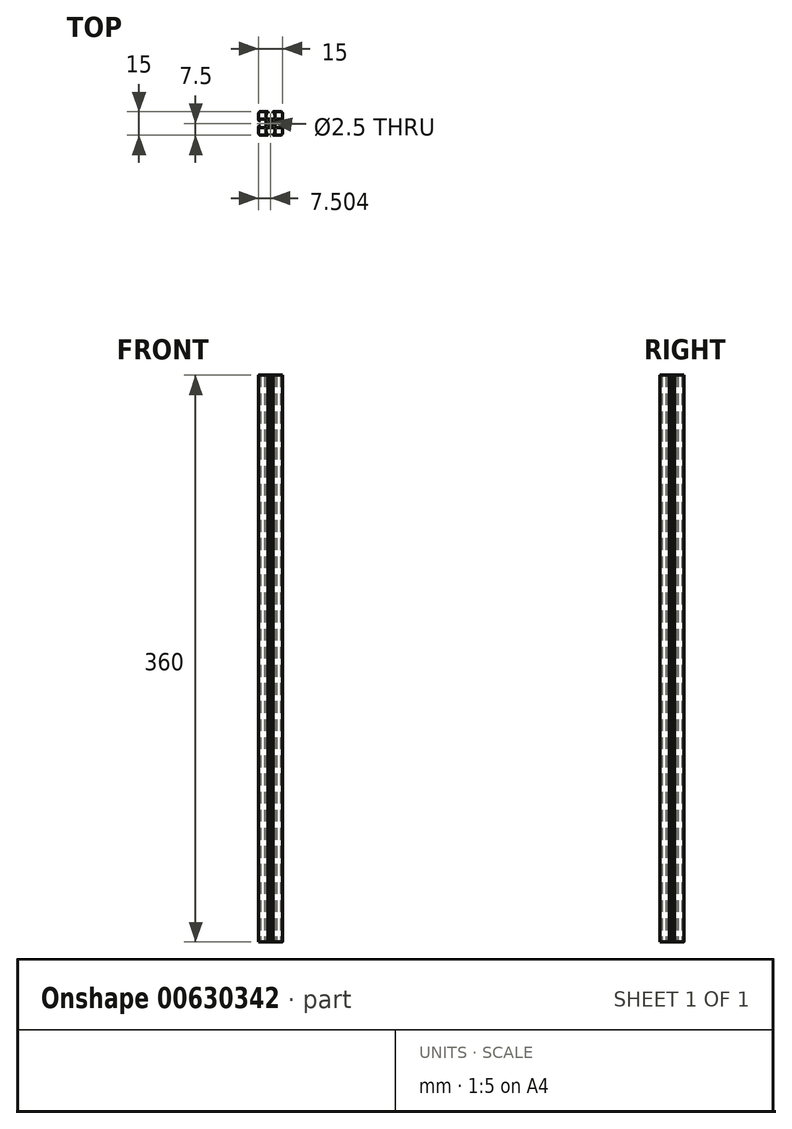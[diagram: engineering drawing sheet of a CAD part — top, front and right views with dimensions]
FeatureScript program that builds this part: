
annotation { "Feature Type Name" : "Feature", "Feature Type Description" : "" }
export const myFeature = defineFeature(function(context is Context, id is Id, definition is map)
    precondition{}
    {
        {
            var Q0;
            Q0=qCreatedBy(makeId("Top.planeOp"),FACE);
            var sketch = newSketch(context, id + "F0", { "sketchPlane" : qUnion([Q0])});
            skLineSegment(sketch, "E0", {"start": v(-5.54, -0.25) * mm, "end": v(-2.91, -0.25) * mm});
            skLineSegment(sketch, "E1", {"start": v(-4.23, -1.56) * mm, "end": v(-4.23, 1.06) * mm});
            skLineSegment(sketch, "E2", {"start": v(-11.73, 6.25) * mm, "end": v(-11.73, 1.75) * mm});
            skArc(sketch, "E3", {"start": v(-11.73, 1.75) * mm, "mid": v(-11.64, 1.54) * mm, "end": v(-11.43, 1.45) * mm});
            skLineSegment(sketch, "E4", {"start": v(-11.43, 1.45) * mm, "end": v(-10.63, 1.45) * mm});
            skLineSegment(sketch, "E5", {"start": v(-10.63, 1.45) * mm, "end": v(-10.63, 2.6) * mm});
            skLineSegment(sketch, "E6", {"start": v(-10.63, 2.6) * mm, "end": v(-8.03, 2.6) * mm});
            skLineSegment(sketch, "E7", {"start": v(-8.03, 2.6) * mm, "end": v(-7.03, 1.6) * mm});
            skLineSegment(sketch, "E8", {"start": v(-7.03, 1.6) * mm, "end": v(-7.03, 0.27) * mm});
            skLineSegment(sketch, "E9", {"start": v(-7.03, 0.27) * mm, "end": v(-6.73, -0.25) * mm});
            skLineSegment(sketch, "E10", {"start": v(-6.73, -0.25) * mm, "end": v(-7.03, -0.77) * mm});
            skLineSegment(sketch, "E11", {"start": v(-7.03, -0.77) * mm, "end": v(-7.03, -2.1) * mm});
            skLineSegment(sketch, "E12", {"start": v(-7.03, -2.1) * mm, "end": v(-8.03, -3.1) * mm});
            skLineSegment(sketch, "E13", {"start": v(-8.03, -3.1) * mm, "end": v(-10.63, -3.1) * mm});
            skLineSegment(sketch, "E14", {"start": v(-10.63, -3.1) * mm, "end": v(-10.63, -1.95) * mm});
            skLineSegment(sketch, "E15", {"start": v(-10.63, -1.95) * mm, "end": v(-11.43, -1.95) * mm});
            skArc(sketch, "E16", {"start": v(-11.43, -1.95) * mm, "mid": v(-11.64, -2.04) * mm, "end": v(-11.73, -2.25) * mm});
            skLineSegment(sketch, "E17", {"start": v(-11.73, -2.25) * mm, "end": v(-11.73, -6.75) * mm});
            skArc(sketch, "E18", {"start": v(-11.73, -6.75) * mm, "mid": v(-11.43, -7.46) * mm, "end": v(-10.73, -7.75) * mm});
            skLineSegment(sketch, "E19", {"start": v(-10.73, -7.75) * mm, "end": v(-6.23, -7.75) * mm});
            skArc(sketch, "E20", {"start": v(-6.23, -7.75) * mm, "mid": v(-6.01, -7.66) * mm, "end": v(-5.93, -7.45) * mm});
            skLineSegment(sketch, "E21", {"start": v(-5.93, -7.45) * mm, "end": v(-5.93, -6.65) * mm});
            skLineSegment(sketch, "E22", {"start": v(-5.93, -6.65) * mm, "end": v(-7.08, -6.65) * mm});
            skLineSegment(sketch, "E23", {"start": v(-7.08, -6.65) * mm, "end": v(-7.08, -4.05) * mm});
            skLineSegment(sketch, "E24", {"start": v(-7.08, -4.05) * mm, "end": v(-6.08, -3.05) * mm});
            skLineSegment(sketch, "E25", {"start": v(-6.08, -3.05) * mm, "end": v(-4.75, -3.05) * mm});
            skLineSegment(sketch, "E26", {"start": v(-4.75, -3.05) * mm, "end": v(-4.23, -2.75) * mm});
            skLineSegment(sketch, "E27", {"start": v(-4.23, -2.75) * mm, "end": v(-3.7, -3.05) * mm});
            skLineSegment(sketch, "E28", {"start": v(-3.7, -3.05) * mm, "end": v(-2.38, -3.05) * mm});
            skLineSegment(sketch, "E29", {"start": v(-2.38, -3.05) * mm, "end": v(-1.38, -4.05) * mm});
            skLineSegment(sketch, "E30", {"start": v(-1.38, -4.05) * mm, "end": v(-1.38, -6.65) * mm});
            skLineSegment(sketch, "E31", {"start": v(-1.38, -6.65) * mm, "end": v(-2.53, -6.65) * mm});
            skLineSegment(sketch, "E32", {"start": v(-2.53, -6.65) * mm, "end": v(-2.53, -7.45) * mm});
            skArc(sketch, "E33", {"start": v(-2.53, -7.45) * mm, "mid": v(-2.44, -7.66) * mm, "end": v(-2.23, -7.75) * mm});
            skLineSegment(sketch, "E34", {"start": v(-2.23, -7.75) * mm, "end": v(2.27, -7.75) * mm});
            skArc(sketch, "E35", {"start": v(2.27, -7.75) * mm, "mid": v(2.98, -7.46) * mm, "end": v(3.27, -6.75) * mm});
            skLineSegment(sketch, "E36", {"start": v(3.27, -6.75) * mm, "end": v(3.27, -2.25) * mm});
            skArc(sketch, "E37", {"start": v(3.27, -2.25) * mm, "mid": v(3.19, -2.04) * mm, "end": v(2.97, -1.95) * mm});
            skLineSegment(sketch, "E38", {"start": v(2.97, -1.95) * mm, "end": v(2.17, -1.95) * mm});
            skLineSegment(sketch, "E39", {"start": v(2.17, -1.95) * mm, "end": v(2.17, -3.1) * mm});
            skLineSegment(sketch, "E40", {"start": v(2.17, -3.1) * mm, "end": v(-0.43, -3.1) * mm});
            skLineSegment(sketch, "E41", {"start": v(-0.43, -3.1) * mm, "end": v(-1.43, -2.1) * mm});
            skLineSegment(sketch, "E42", {"start": v(-1.43, -2.1) * mm, "end": v(-1.43, -0.77) * mm});
            skLineSegment(sketch, "E43", {"start": v(-1.43, -0.77) * mm, "end": v(-1.73, -0.25) * mm});
            skLineSegment(sketch, "E44", {"start": v(-1.73, -0.25) * mm, "end": v(-1.43, 0.27) * mm});
            skLineSegment(sketch, "E45", {"start": v(-1.43, 0.27) * mm, "end": v(-1.43, 1.6) * mm});
            skLineSegment(sketch, "E46", {"start": v(-1.43, 1.6) * mm, "end": v(-0.43, 2.6) * mm});
            skLineSegment(sketch, "E47", {"start": v(-0.43, 2.6) * mm, "end": v(2.17, 2.6) * mm});
            skLineSegment(sketch, "E48", {"start": v(2.17, 2.6) * mm, "end": v(2.17, 1.45) * mm});
            skLineSegment(sketch, "E49", {"start": v(2.17, 1.45) * mm, "end": v(2.97, 1.45) * mm});
            skArc(sketch, "E50", {"start": v(2.97, 1.45) * mm, "mid": v(3.19, 1.54) * mm, "end": v(3.27, 1.75) * mm});
            skLineSegment(sketch, "E51", {"start": v(3.27, 1.75) * mm, "end": v(3.27, 6.25) * mm});
            skArc(sketch, "E52", {"start": v(3.27, 6.25) * mm, "mid": v(2.98, 6.96) * mm, "end": v(2.27, 7.25) * mm});
            skLineSegment(sketch, "E53", {"start": v(2.27, 7.25) * mm, "end": v(-2.23, 7.25) * mm});
            skArc(sketch, "E54", {"start": v(-2.23, 7.25) * mm, "mid": v(-2.44, 7.16) * mm, "end": v(-2.53, 6.95) * mm});
            skLineSegment(sketch, "E55", {"start": v(-2.53, 6.95) * mm, "end": v(-2.53, 6.15) * mm});
            skLineSegment(sketch, "E56", {"start": v(-2.53, 6.15) * mm, "end": v(-1.38, 6.15) * mm});
            skLineSegment(sketch, "E57", {"start": v(-1.38, 6.15) * mm, "end": v(-1.38, 3.55) * mm});
            skLineSegment(sketch, "E58", {"start": v(-1.38, 3.55) * mm, "end": v(-2.38, 2.55) * mm});
            skLineSegment(sketch, "E59", {"start": v(-2.38, 2.55) * mm, "end": v(-3.7, 2.55) * mm});
            skLineSegment(sketch, "E60", {"start": v(-3.7, 2.55) * mm, "end": v(-4.23, 2.25) * mm});
            skLineSegment(sketch, "E61", {"start": v(-4.23, 2.25) * mm, "end": v(-4.75, 2.55) * mm});
            skLineSegment(sketch, "E62", {"start": v(-4.75, 2.55) * mm, "end": v(-6.08, 2.55) * mm});
            skLineSegment(sketch, "E63", {"start": v(-6.08, 2.55) * mm, "end": v(-7.08, 3.55) * mm});
            skLineSegment(sketch, "E64", {"start": v(-7.08, 3.55) * mm, "end": v(-7.08, 6.15) * mm});
            skLineSegment(sketch, "E65", {"start": v(-7.08, 6.15) * mm, "end": v(-5.93, 6.15) * mm});
            skLineSegment(sketch, "E66", {"start": v(-5.93, 6.15) * mm, "end": v(-5.93, 6.95) * mm});
            skArc(sketch, "E67", {"start": v(-5.93, 6.95) * mm, "mid": v(-6.01, 7.16) * mm, "end": v(-6.23, 7.25) * mm});
            skLineSegment(sketch, "E68", {"start": v(-6.23, 7.25) * mm, "end": v(-10.73, 7.25) * mm});
            skCircle(sketch, "E69", {"center": v(-4.23, -0.25) * mm, "radius": 1.25 * mm});
            skArc(sketch, "E70", {"start": v(-10.73, 7.25) * mm, "mid": v(-11.43, 6.96) * mm, "end": v(-11.73, 6.25) * mm});
            skSolve(sketch);
        }
        {
            var Q0;
            Q0=makeQuery(id+"F0.imprint","IMPRINT",FACE,{"disambiguationData":[TD([[makeQuery(id+"F0.imprint","IMPRINT",EDGE,{"derivedFrom":sQuery(id+"F0.wireOp",EDGE,"E2")}),1.0]])]});
            extrude(context, id + "F1", {"entities" : qUnion([Q0]), "depth" : 360 * mm, "offsetDistance" : 25 * mm});
        }
    });
